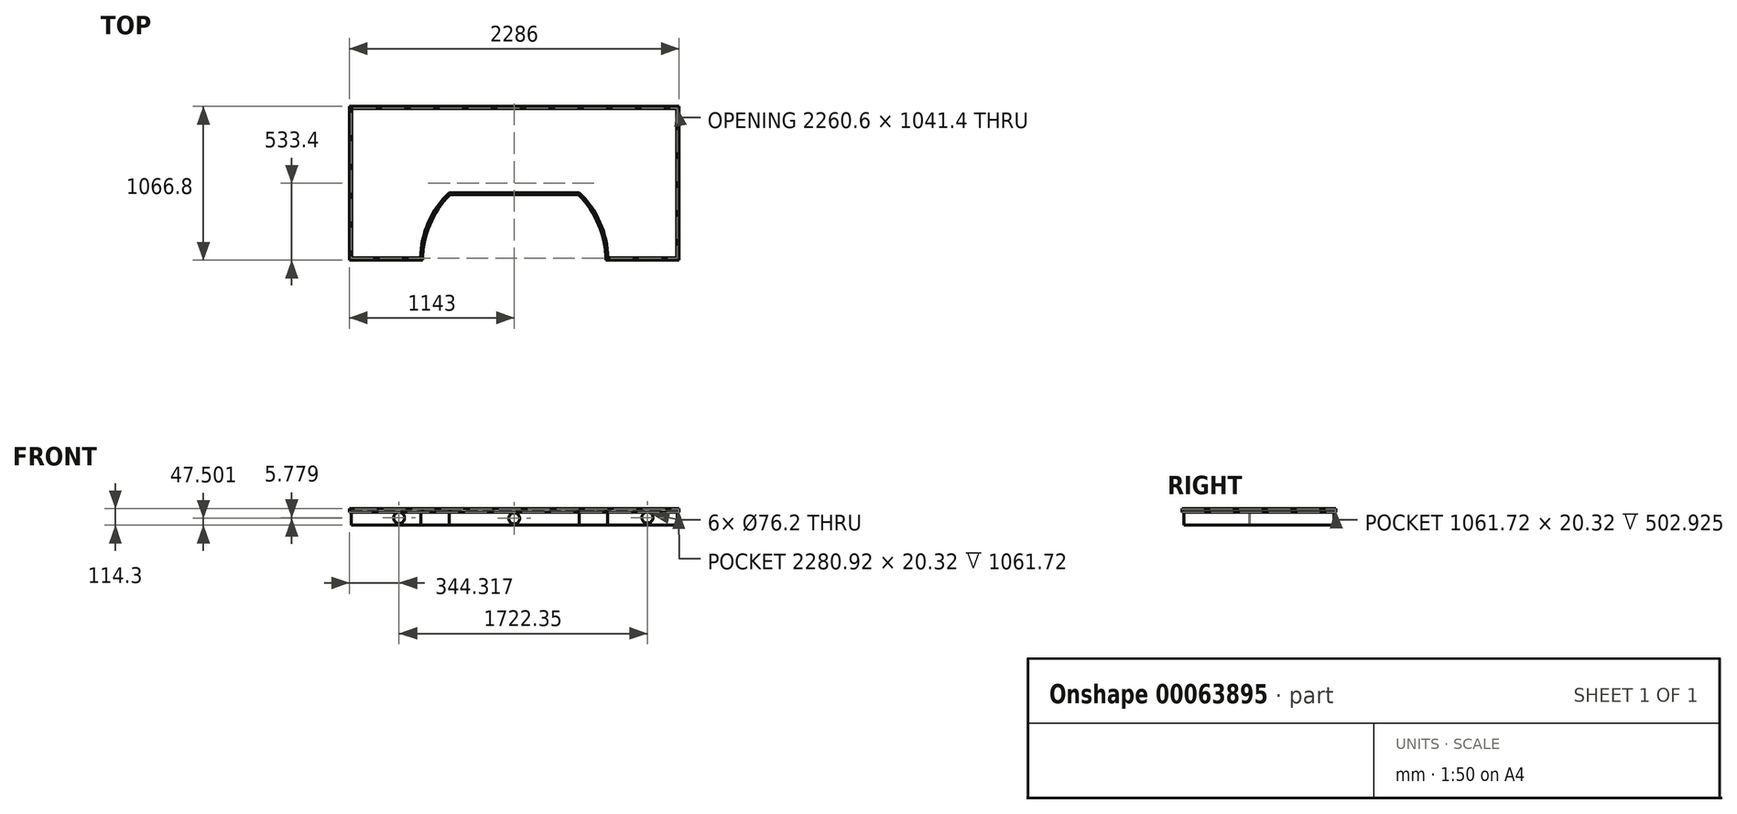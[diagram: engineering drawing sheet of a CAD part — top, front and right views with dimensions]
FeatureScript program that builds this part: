
annotation { "Feature Type Name" : "Feature", "Feature Type Description" : "" }
export const myFeature = defineFeature(function(context is Context, id is Id, definition is map)
    precondition{}
    {
        {
            var Q0;
            Q0=qCreatedBy(makeId("Top.planeOp"),FACE);
            var sketch = newSketch(context, id + "F0", { "sketchPlane" : qUnion([Q0])});
            skLineSegment(sketch, "E0.top", {"start": v(-1143, 609.6) * mm, "end": v(0, 609.6) * mm});
            skLineSegment(sketch, "E0.left", {"start": v(-1143, 0) * mm, "end": v(-1143, 609.6) * mm});
            skPoint(sketch, "E1.start.orphan", {"position": v(0, 177.8) * mm});
            skLineSegment(sketch, "E2", {"start": v(-1143, 0) * mm, "end": v(-1143, -457.2) * mm});
            skLineSegment(sketch, "E3", {"start": v(-1143, -457.2) * mm, "end": v(-635, -457.2) * mm});
            skLineSegment(sketch, "E4", {"start": v(-635, -457.2) * mm, "end": v(-635, -457.2) * mm});
            skArc(sketch, "E5", {"start": v(3.18, 177.8) * mm, "mid": v(0, 177.8) * mm, "end": v(-3.18, 177.8) * mm});
            skPoint(sketch, "E6.MirrorP", {"position": v(3.17, 177.64) * mm});
            skLineSegment(sketch, "E7.MirrorCS", {"start": v(634.96, -438.3) * mm, "end": v(634.96, -438.3) * mm});
            skLineSegment(sketch, "E8.MirrorCS", {"start": v(1135.13, -438.3) * mm, "end": v(1132.5, -438.3) * mm});
            skPoint(sketch, "E9.end.orphan", {"position": v(-585.44, -211.27) * mm});
            skPoint(sketch, "E10.orphan", {"position": v(-444.5, -3.72) * mm});
            skPoint(sketch, "E11.MirrorCS.end.orphan", {"position": v(0, 609.6) * mm});
            skLineSegment(sketch, "E12", {"start": v(0, 609.6) * mm, "end": v(0, -457.2) * mm, "construction": true});
            skLineSegment(sketch, "E13.MirrorCS", {"start": v(1143, 0) * mm, "end": v(1143, 609.6) * mm});
            skLineSegment(sketch, "E14.MirrorCS", {"start": v(1143, 0) * mm, "end": v(1143, -457.2) * mm});
            skLineSegment(sketch, "E15.MirrorCS", {"start": v(1143, -457.2) * mm, "end": v(635, -457.2) * mm});
            skArc(sketch, "E16.MirrorCS", {"start": v(-3.18, 177.8) * mm, "mid": v(0, 177.8) * mm, "end": v(3.18, 177.8) * mm});
            skPoint(sketch, "E17.MirrorP", {"position": v(-3.17, 177.64) * mm});
            skLineSegment(sketch, "E18.MirrorCS", {"start": v(1143, 609.6) * mm, "end": v(0, 609.6) * mm});
            skPoint(sketch, "E19.MirrorP", {"position": v(585.44, -211.27) * mm});
            skPoint(sketch, "E20.MirrorP", {"position": v(444.5, -3.72) * mm});
            skLineSegment(sketch, "E21", {"start": v(-444.5, -3.72) * mm, "end": v(444.5, -3.72) * mm});
            skArc(sketch, "E22.trimOffspring", {"start": v(-444.5, -3.72) * mm, "mid": v(-585.44, -211.27) * mm, "end": v(-635, -457.2) * mm});
            skArc(sketch, "E23.trimOffspring", {"start": v(444.5, -3.72) * mm, "mid": v(585.44, -211.27) * mm, "end": v(635, -457.2) * mm});
            skLineSegment(sketch, "E24", {"start": v(585.44, -211.27) * mm, "end": v(658.35, -177.84) * mm, "construction": true});
            skPoint(sketch, "E25.orphan", {"position": v(-658.35, -177.84) * mm});
            skSolve(sketch);
        }
        {
            var Q0;
            Q0=makeQuery(id+"F0.imprint","IMPRINT",FACE,{"disambiguationData":[TD([[makeQuery(id+"F0.imprint","IMPRINT",EDGE,{"derivedFrom":sQuery(id+"F0.wireOp",EDGE,"E0.top")}),-1.0]])]});
            extrude(context, id + "F1", {"entities" : qUnion([Q0]), "depth" : 25.4 * mm});
        }
        {
            var Q0;
            Q0=qSketchRegion(id+"F0",true);
            extrude(context, id + "F2", {"entities" : qUnion([Q0]), "operationType" : NewBodyOperationType.ADD, "depth" : 25.4 * mm});
        }
        {
            var Q0;
            Q0=makeQuery(id+"F1.opExtrude","CAP_FACE",FACE,{"disambiguationData":[OSD([sQuery(id+"F0.wireOp",EDGE,"E0.top"),sQuery(id+"F0.wireOp",EDGE,"E0.left"),sQuery(id+"F0.wireOp",EDGE,"E2"),sQuery(id+"F0.wireOp",EDGE,"E3"),sQuery(id+"F0.wireOp",EDGE,"E13.MirrorCS"),sQuery(id+"F0.wireOp",EDGE,"E14.MirrorCS"),sQuery(id+"F0.wireOp",EDGE,"E15.MirrorCS"),sQuery(id+"F0.wireOp",EDGE,"E18.MirrorCS"),sQuery(id+"F0.wireOp",EDGE,"E21"),sQuery(id+"F0.wireOp",EDGE,"E22.trimOffspring"),sQuery(id+"F0.wireOp",EDGE,"E23.trimOffspring")])],"isStart":false});
            var Q1;
            Q1=makeQuery(id+"F1.opExtrude","SWEPT_BODY",BODY,{"disambiguationData":[OSD([sQuery(id+"F0.wireOp",EDGE,"E0.top"),sQuery(id+"F0.wireOp",EDGE,"E0.left"),sQuery(id+"F0.wireOp",EDGE,"E2"),sQuery(id+"F0.wireOp",EDGE,"E3"),sQuery(id+"F0.wireOp",EDGE,"E13.MirrorCS"),sQuery(id+"F0.wireOp",EDGE,"E14.MirrorCS"),sQuery(id+"F0.wireOp",EDGE,"E15.MirrorCS"),sQuery(id+"F0.wireOp",EDGE,"E18.MirrorCS"),sQuery(id+"F0.wireOp",EDGE,"E21"),sQuery(id+"F0.wireOp",EDGE,"E22.trimOffspring"),sQuery(id+"F0.wireOp",EDGE,"E23.trimOffspring")])]});
            shell(context, id + "F3", {"entities" : qUnion([Q0]), "parts" : qUnion([Q1]), "thickness" : 12.7 * mm});
        }
        {
            var Q0;
            Q0=makeQuery(id+"F3.opShell","OFFSET_FACE",FACE,{"disambiguationData":[OSD([sQuery(id+"F0.wireOp",EDGE,"E0.top"),sQuery(id+"F0.wireOp",EDGE,"E0.left"),sQuery(id+"F0.wireOp",EDGE,"E2"),sQuery(id+"F0.wireOp",EDGE,"E3"),sQuery(id+"F0.wireOp",EDGE,"E13.MirrorCS"),sQuery(id+"F0.wireOp",EDGE,"E14.MirrorCS"),sQuery(id+"F0.wireOp",EDGE,"E15.MirrorCS"),sQuery(id+"F0.wireOp",EDGE,"E18.MirrorCS"),sQuery(id+"F0.wireOp",EDGE,"E21"),sQuery(id+"F0.wireOp",EDGE,"E22.trimOffspring"),sQuery(id+"F0.wireOp",EDGE,"E23.trimOffspring")])]});
            extrude(context, id + "F4", {"entities" : qUnion([Q0]), "operationType" : NewBodyOperationType.ADD, "oppositeDirection" : true, "depth" : 101.6 * mm});
        }
        {
            var Q0;
            Q0=makeQuery(id+"F3.opShell","OFFSET_FACE",FACE,{"disambiguationData":[OSD([sQuery(id+"F0.wireOp",EDGE,"E0.top"),sQuery(id+"F0.wireOp",EDGE,"E0.left"),sQuery(id+"F0.wireOp",EDGE,"E2"),sQuery(id+"F0.wireOp",EDGE,"E3"),sQuery(id+"F0.wireOp",EDGE,"E13.MirrorCS"),sQuery(id+"F0.wireOp",EDGE,"E14.MirrorCS"),sQuery(id+"F0.wireOp",EDGE,"E15.MirrorCS"),sQuery(id+"F0.wireOp",EDGE,"E18.MirrorCS"),sQuery(id+"F0.wireOp",EDGE,"E21"),sQuery(id+"F0.wireOp",EDGE,"E22.trimOffspring"),sQuery(id+"F0.wireOp",EDGE,"E23.trimOffspring")])]});
            shell(context, id + "F5", {"entities" : qUnion([Q0]), "thickness" : 2.54 * mm});
        }
        {
            var Q0;
            Q0=makeQuery(id+"F4.opExtrude","SWEPT_FACE",FACE,{"disambiguationData":[OSD([sQuery(id+"F0.wireOp",EDGE,"E0.top"),sQuery(id+"F0.wireOp",EDGE,"E18.MirrorCS")])]});
            var sketch = newSketch(context, id + "F6", { "sketchPlane" : qUnion([Q0])});
            skCircle(sketch, "E26", {"center": v(-923.67, -35.62) * mm, "radius": 53.28 * mm});
            skCircle(sketch, "E27", {"center": v(798.68, -37.41) * mm, "radius": 51.49 * mm});
            skCircle(sketch, "E28", {"center": v(0, -41.4) * mm, "radius": 47.58 * mm});
            skPoint(sketch, "E28.centerSnap0", {"position": v(0, 0) * mm});
            skSolve(sketch);
        }
        {
            var Q0;
            Q0=sQuery(id+"F6.wireOp",VERTEX,"E26.center");
            var Q1;
            Q1=sQuery(id+"F6.wireOp",VERTEX,"E28.center");
            var Q2;
            Q2=sQuery(id+"F6.wireOp",VERTEX,"E27.center");
            var Q3;
            Q3=makeQuery(id+"F1.opExtrude","SWEPT_BODY",BODY,{"disambiguationData":[OSD([sQuery(id+"F0.wireOp",EDGE,"E0.top"),sQuery(id+"F0.wireOp",EDGE,"E0.left"),sQuery(id+"F0.wireOp",EDGE,"E2"),sQuery(id+"F0.wireOp",EDGE,"E3"),sQuery(id+"F0.wireOp",EDGE,"E13.MirrorCS"),sQuery(id+"F0.wireOp",EDGE,"E14.MirrorCS"),sQuery(id+"F0.wireOp",EDGE,"E15.MirrorCS"),sQuery(id+"F0.wireOp",EDGE,"E18.MirrorCS"),sQuery(id+"F0.wireOp",EDGE,"E21"),sQuery(id+"F0.wireOp",EDGE,"E22.trimOffspring"),sQuery(id+"F0.wireOp",EDGE,"E23.trimOffspring")])]});
            hole(context, id + "F7", {"style" : HoleStyle.SIMPLE, "holeDiameter" : 76.2 * mm, "endStyle" : HoleEndStyle.THROUGH, "locations" : qUnion([Q0, Q1, Q2]), "scope" : qUnion([Q3])});
        }
    });
